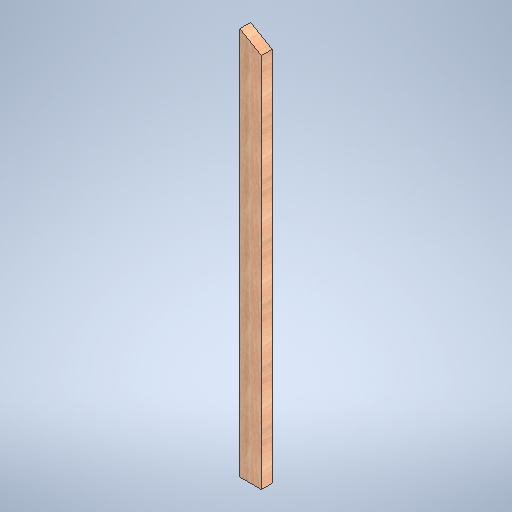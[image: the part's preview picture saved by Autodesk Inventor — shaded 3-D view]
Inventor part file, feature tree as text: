
AUTODESK INVENTOR PART (.ipt)
format: ipt  version: 2025 (Build 290162000, 162)  size: 294,400 bytes
history: native  units: in
note: dims shown in document units (in); Inventor stores cm internally (conversion verified against a paired STEP export)
features: extrude x1, sketch x1
ambient origin geometry x8: Origin, YZ Plane, XZ Plane, XY Plane, X Axis, Y Axis, Z Axis, Center Point
bodies: Solid1 (feature_tree)
feature tree (2):
  extrude  "Extrusion1"  [1 undecoded]
  sketch  "Sketch1"  dims[d3=2.0in d4=0.0in]
note: 1 required parameter value undecoded (feature->parameter linkage not recoverable at this tier; creation-order binding heuristic only, values carry confidence <= 0.55)
